# Revit family: FU_Table_Sandler_MacsTable 216-23
name_source: partatom
category: Furniture
units: mm (PartAtom-declared; Revit-internal decimal feet)

## family parameters
Always vertical = Yes
Cut with Voids When Loaded = No
OmniClass Number = 23.40.20.00
OmniClass Title = General Furniture and Specialties
Room Calculation Point = No
Shared = No
Work Plane-Based = No

## types (1)
- Mac's Table 216.23
    Default Elevation = 0 mm  [stored 0 ft]
    Depth = 1300 mm  [stored 4.26509 ft]
    Description = Table with base in high density polyurethane, Walnut or Oak veneer. The five base elements can be arranged in two combinations by joining with a steel component. 12 mm/0.5″ semi-transparent gray glass top. Size: 130 cm/51″ dia. Base elements can be single- or multi colored.
    Height = 740 mm  [stored 2.42782 ft]
    Manufacturer = Sandler
    Model = Mac's Table 216.23
    URL = https://www.sandlerseating.com
    Width = 1300 mm  [stored 4.26509 ft]

note: [stored X ft] marks values corroborated as IEEE doubles in the binary element streams (Revit-internal decimal feet)

## geometry (parser evidence)
native form markers: Sweep x5
no freeform markers — native parametric forms only
